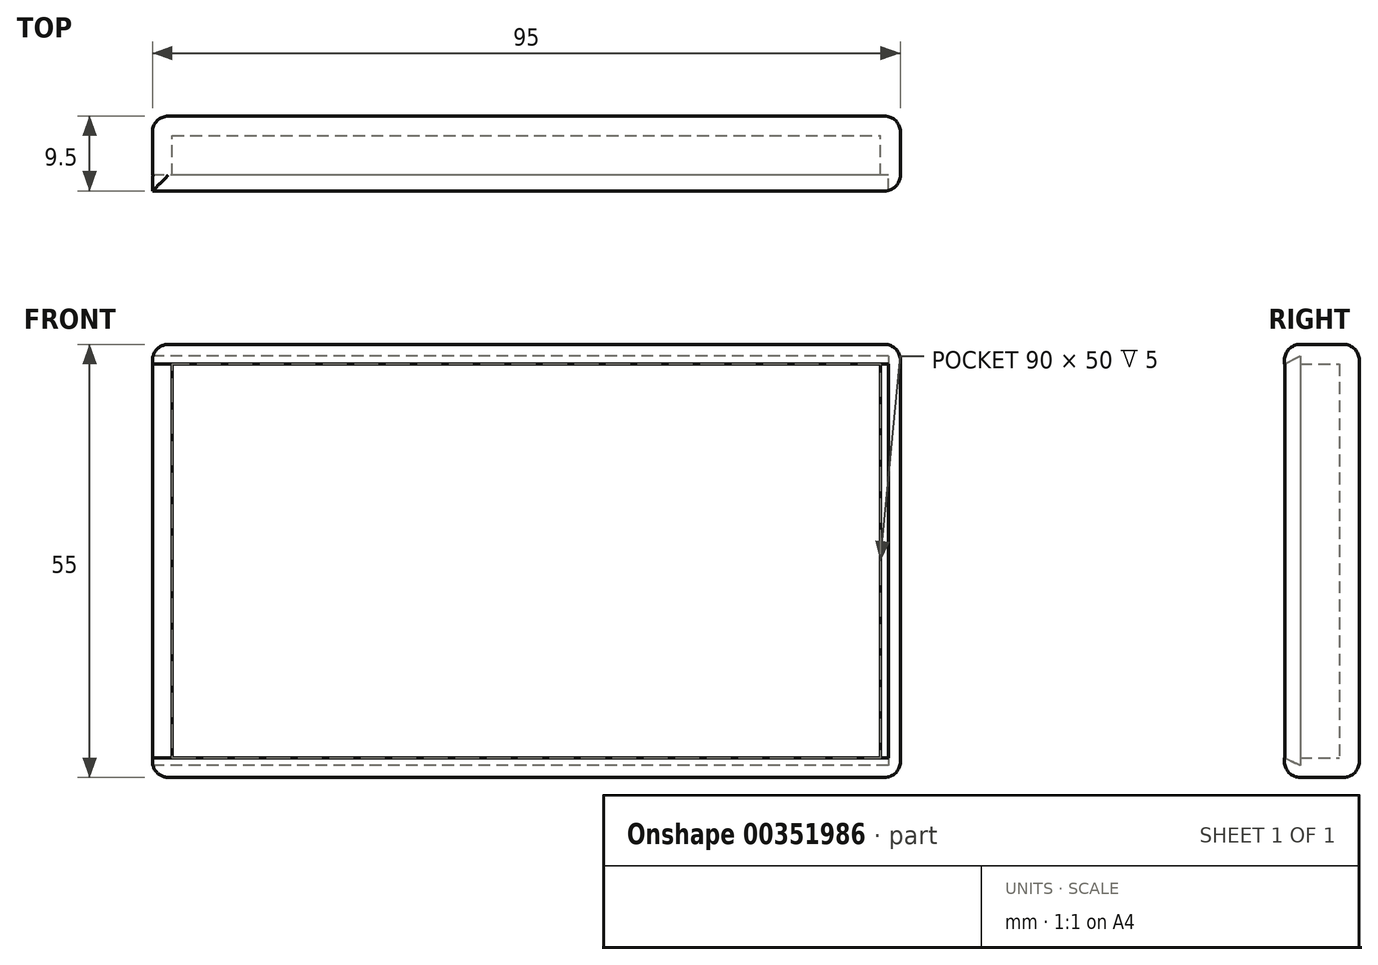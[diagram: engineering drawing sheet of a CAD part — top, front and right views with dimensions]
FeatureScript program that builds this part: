
annotation { "Feature Type Name" : "Feature", "Feature Type Description" : "" }
export const myFeature = defineFeature(function(context is Context, id is Id, definition is map)
    precondition{}
    {
        {
            var Q0;
            Q0=qCreatedBy(makeId("Front.planeOp"),FACE);
            var sketch = newSketch(context, id + "F0", { "sketchPlane" : qUnion([Q0])});
            skLineSegment(sketch, "E0.bottom", {"start": v(-45, 25) * mm, "end": v(45, 25) * mm});
            skLineSegment(sketch, "E0.top", {"start": v(-45, -25) * mm, "end": v(45, -25) * mm});
            skLineSegment(sketch, "E0.left", {"start": v(-45, 25) * mm, "end": v(-45, -25) * mm});
            skLineSegment(sketch, "E0.right", {"start": v(45, 25) * mm, "end": v(45, -25) * mm});
            skSolve(sketch);
        }
        {
            var Q0;
            Q0=makeQuery(id+"F0.imprint","IMPRINT",FACE,{"disambiguationData":[TD([[makeQuery(id+"F0.imprint","IMPRINT",EDGE,{"derivedFrom":sQuery(id+"F0.wireOp",EDGE,"E0.bottom")}),-1.0]])]});
            extrude(context, id + "F1", {"entities" : qUnion([Q0]), "depth" : 5 * mm});
        }
        {
            var Q0;
            Q0=makeQuery(id+"F1.opExtrude","CAP_FACE",FACE,{"disambiguationData":[OSD([sQuery(id+"F0.wireOp",EDGE,"E0.bottom"),sQuery(id+"F0.wireOp",EDGE,"E0.top"),sQuery(id+"F0.wireOp",EDGE,"E0.left"),sQuery(id+"F0.wireOp",EDGE,"E0.right")])],"isStart":false});
            shell(context, id + "F2", {"entities" : qUnion([Q0]), "thickness" : 2.5 * mm, "oppositeDirection" : true});
        }
        {
            var Q0;
            Q0=makeQuery(id+"F1.opExtrude","CAP_FACE",FACE,{"disambiguationData":[OSD([sQuery(id+"F0.wireOp",EDGE,"E0.bottom"),sQuery(id+"F0.wireOp",EDGE,"E0.top"),sQuery(id+"F0.wireOp",EDGE,"E0.left"),sQuery(id+"F0.wireOp",EDGE,"E0.right")])],"isStart":true});
            var Q1;
            Q1=makeQuery(id+"F1.opExtrude","SWEPT_EDGE",EDGE,{"disambiguationData":[OSD([sQuery(id+"F0.wireOp",EDGE,"E0.top"),sQuery(id+"F0.wireOp",EDGE,"E0.right")])]});
            var Q2;
            Q2=makeQuery(id+"F1.opExtrude","SWEPT_EDGE",EDGE,{"disambiguationData":[OSD([sQuery(id+"F0.wireOp",EDGE,"E0.bottom"),sQuery(id+"F0.wireOp",EDGE,"E0.right")])]});
            fillet(context, id + "F3", {"entities" : qUnion([Q0, Q1, Q2]), "radius" : 2 * mm, "tangentPropagation" : true, "allowEdgeOverflow" : false});
        }
        {
            var Q0;
            Q0=makeQuery(id+"F1.opExtrude","CAP_FACE",FACE,{"disambiguationData":[OSD([sQuery(id+"F0.wireOp",EDGE,"E0.bottom"),sQuery(id+"F0.wireOp",EDGE,"E0.top"),sQuery(id+"F0.wireOp",EDGE,"E0.left"),sQuery(id+"F0.wireOp",EDGE,"E0.right")])],"isStart":false});
            var sketch = newSketch(context, id + "F4", { "sketchPlane" : qUnion([Q0])});
            skLineSegment(sketch, "E1.bottom", {"start": v(-45, -25) * mm, "end": v(45, -25) * mm});
            skLineSegment(sketch, "E1.top", {"start": v(-45, -27.5) * mm, "end": v(47.5, -27.5) * mm});
            skLineSegment(sketch, "E1.right", {"start": v(47.5, -25) * mm, "end": v(47.5, -27.5) * mm});
            skLineSegment(sketch, "E2.top", {"start": v(47.5, 27.5) * mm, "end": v(45, 27.5) * mm});
            skLineSegment(sketch, "E2.left", {"start": v(47.5, -25) * mm, "end": v(47.5, 27.5) * mm});
            skLineSegment(sketch, "E2.right", {"start": v(45, -25) * mm, "end": v(45, 25) * mm});
            skLineSegment(sketch, "E3.bottom", {"start": v(45, 27.5) * mm, "end": v(-45.5, 27.5) * mm});
            skLineSegment(sketch, "E3.top", {"start": v(45, 25) * mm, "end": v(-45, 25) * mm});
            skLineSegment(sketch, "E4.bottom", {"start": v(-47.5, 27.5) * mm, "end": v(-45.5, 27.5) * mm});
            skLineSegment(sketch, "E4.top", {"start": v(-47.5, 25) * mm, "end": v(-45, 25) * mm});
            skLineSegment(sketch, "E4.left", {"start": v(-47.5, 27.5) * mm, "end": v(-47.5, 25) * mm});
            skLineSegment(sketch, "E5.bottom", {"start": v(-47.5, -27.5) * mm, "end": v(-45.5, -27.5) * mm});
            skLineSegment(sketch, "E5.top", {"start": v(-47.5, -25) * mm, "end": v(-45, -25) * mm});
            skLineSegment(sketch, "E5.left", {"start": v(-47.5, -27.5) * mm, "end": v(-47.5, -25) * mm});
            skSolve(sketch);
        }
        {
            var Q0;
            Q0=makeQuery(id+"F4.imprint","IMPRINT",FACE,{"disambiguationData":[TD([[makeQuery(id+"F4.imprint","IMPRINT",EDGE,{"derivedFrom":sQuery(id+"F4.wireOp",EDGE,"E1.bottom")}),-1.0]])]});
            extrude(context, id + "F5", {"entities" : qUnion([Q0]), "operationType" : NewBodyOperationType.ADD, "depth" : 2 * mm});
        }
        {
            var Q0;
            Q0=makeQuery(id+"F5.boolean.opBoolean","MERGE",FACE,{"derivedFrom":[makeQuery(id+"F1.opExtrude","SWEPT_FACE",FACE,{"disambiguationData":[OSD([sQuery(id+"F0.wireOp",EDGE,"E0.left")])]}),makeQuery(id+"F5.opExtrude","SWEPT_FACE",FACE,{"disambiguationData":[OSD([sQuery(id+"F4.wireOp",EDGE,"E4.left")])]}),makeQuery(id+"F5.opExtrude","SWEPT_FACE",FACE,{"disambiguationData":[OSD([sQuery(id+"F4.wireOp",EDGE,"E5.left")])]})]});
            var sketch = newSketch(context, id + "F6", { "sketchPlane" : qUnion([Q0])});
            skLineSegment(sketch, "E6.left", {"start": v(7, 25) * mm, "end": v(7, -25) * mm});
            skLineSegment(sketch, "E6.right", {"start": v(5, 25) * mm, "end": v(5, -25) * mm});
            skLineSegment(sketch, "E7", {"start": v(5, 25) * mm, "end": v(5, 26) * mm});
            skLineSegment(sketch, "E8", {"start": v(5, -25) * mm, "end": v(5, -26) * mm});
            skLineSegment(sketch, "E9", {"start": v(7, 25) * mm, "end": v(5, 26) * mm});
            skLineSegment(sketch, "E10", {"start": v(7, -25) * mm, "end": v(5, -26) * mm});
            skSolve(sketch);
        }
        {
            var Q0;
            Q0=makeQuery(id+"F6.imprint","IMPRINT",FACE,{"disambiguationData":[TD([[makeQuery(id+"F6.imprint","IMPRINT",EDGE,{"derivedFrom":sQuery(id+"F6.wireOp",EDGE,"E6.left")}),-1.0]])]});
            var Q1;
            Q1=makeQuery(id+"F6.imprint","IMPRINT",FACE,{"disambiguationData":[TD([[makeQuery(id+"F6.imprint","IMPRINT",EDGE,{"derivedFrom":sQuery(id+"F6.wireOp",EDGE,"E8")}),1.0]])]});
            var Q2;
            Q2=makeQuery(id+"F6.imprint","IMPRINT",FACE,{"disambiguationData":[TD([[makeQuery(id+"F6.imprint","IMPRINT",EDGE,{"derivedFrom":sQuery(id+"F6.wireOp",EDGE,"E7")}),-1.0]])]});
            extrude(context, id + "F7", {"entities" : qUnion([Q0, Q1, Q2]), "operationType" : NewBodyOperationType.REMOVE, "oppositeDirection" : true, "depth" : 93.5 * mm});
        }
        {
            var Q0;
            {var subQ0=sQuery(id+"F0.wireOp",EDGE,"E0.bottom");Q0=makeQuery(id+"F5.boolean.opBoolean","MERGE",FACE,{"derivedFrom":[makeQuery(id+"F1.opExtrude","SWEPT_FACE",FACE,{"disambiguationData":[OSD([subQ0])]}),makeQuery(id+"F5.opExtrude","SWEPT_FACE",FACE,{"disambiguationData":[OSD([subQ0,sQuery(id+"F4.wireOp",EDGE,"E2.top"),sQuery(id+"F4.wireOp",EDGE,"E3.bottom"),sQuery(id+"F4.wireOp",EDGE,"E4.bottom")])]})]});}
            var Q1;
            Q1=makeQuery(id+"F5.boolean.opBoolean","MERGE",EDGE,{"derivedFrom":[makeQuery(id+"F1.opExtrude","SWEPT_EDGE",EDGE,{"disambiguationData":[OSD([sQuery(id+"F0.wireOp",EDGE,"E0.top"),sQuery(id+"F0.wireOp",EDGE,"E0.left")])]}),makeQuery(id+"F5.opExtrude","SWEPT_EDGE",EDGE,{"disambiguationData":[OSD([sQuery(id+"F4.wireOp",EDGE,"E5.bottom"),sQuery(id+"F4.wireOp",EDGE,"E5.left")])]})]});
            fillet(context, id + "F8", {"entities" : qUnion([Q0, Q1]), "radius" : 2 * mm, "tangentPropagation" : true, "allowEdgeOverflow" : false});
        }
    });
